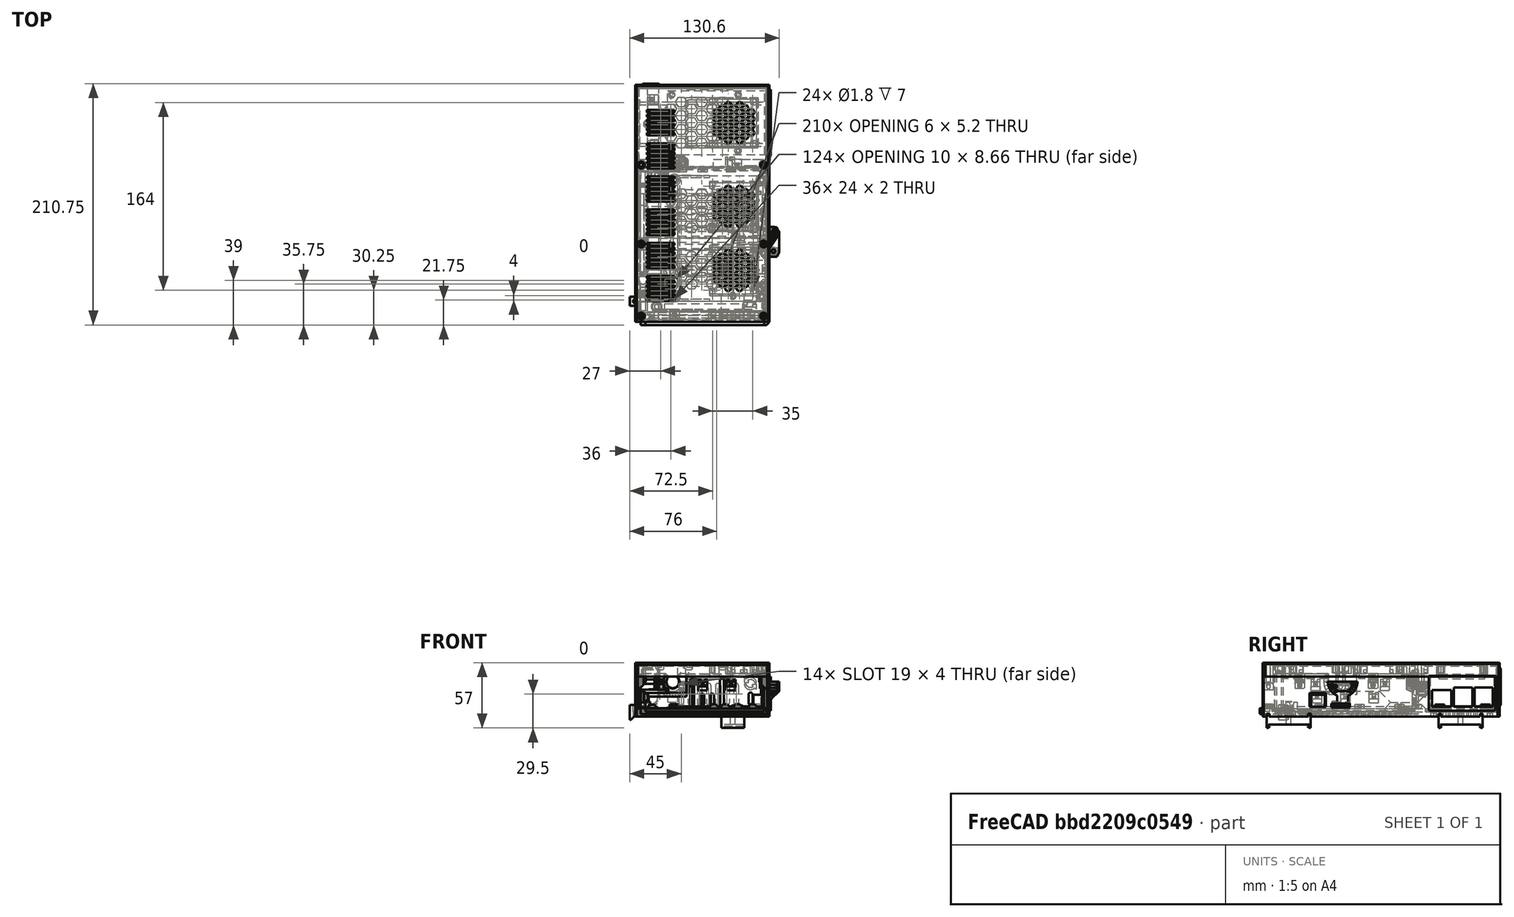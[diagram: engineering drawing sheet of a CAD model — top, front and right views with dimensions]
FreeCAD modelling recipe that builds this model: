
FCSTD DOCUMENT  (FreeCAD 0.18R16146 (Git))
Label: skr-case
License: All rights reserved
LicenseURL: http://en.wikipedia.org/wiki/All_rights_reserved
objects: Part::Feature×95, Part::Box×58, Part::MultiFuse×58, Part::Cylinder×45, Part::Cut×22, Part::Chamfer×17, Mesh::Feature×2, Part::Fillet×1
note: 296 computed .brp shape members not serialized (recipe doc carries the construction recipe); baked Part::Feature solids carry a one-line shape summary decoded from their .brp

FEATURE [Part::Feature] Cut003002  label="din-mount001"
  Placement = pos=(20,-18,-7) rot=(0,-1,0;1.5708rad)
  shape: bbox 20 x 38.4 x 12 mm, 68 faces (baked)
FEATURE [Part::Feature] Cut003002001  label="din-mount002"
  Placement = pos=(20,132,-7) rot=(0,-1,0;1.5708rad)
  shape: bbox 20 x 38.4 x 12 mm, 68 faces (baked)
FEATURE [Part::Box] Box  label="plate"
  AttacherType = Attacher::AttachEngine3D
  Height = 2
  Length = 84.3
  Width = 109.67
FEATURE [Part::Box] Box001  label="usb-pos"
  AttacherType = Attacher::AttachEngine3D
  Height = 10
  Length = 11.3
  Placement = pos=(73,24.11,2) rot=(0,0,1;0rad)
  Width = 11.98
FEATURE [Part::Box] Box002  label="sd-pos"
  AttacherType = Attacher::AttachEngine3D
  Height = 2
  Length = 13.3
  Placement = pos=(73,42.46,2) rot=(0,0,1;0rad)
  Width = 15.03
FEATURE [Part::Cylinder] Cylinder
  Angle = 360
  AttacherType = Attacher::AttachEngine3D
  Height = 10
  Placement = pos=(4.1,105.92,0) rot=(0,0,1;0rad)
  Radius = 1.65
FEATURE [Part::Cylinder] Cylinder001
  Angle = 360
  AttacherType = Attacher::AttachEngine3D
  Height = 10
  Placement = pos=(80.2,105.92,0) rot=(0,0,1;0rad)
  Radius = 1.65
FEATURE [Part::Cylinder] Cylinder002
  Angle = 360
  AttacherType = Attacher::AttachEngine3D
  Height = 10
  Placement = pos=(80.2,4.07,0) rot=(0,0,1;0rad)
  Radius = 1.65
FEATURE [Part::Cylinder] Cylinder003
  Angle = 360
  AttacherType = Attacher::AttachEngine3D
  Height = 10
  Placement = pos=(4.1,4.07,0) rot=(0,0,1;0rad)
  Radius = 1.65
FEATURE [Part::Cylinder] Cylinder004
  Angle = 360
  AttacherType = Attacher::AttachEngine3D
  Height = 10
  Placement = pos=(4.1,4.07,0) rot=(0,0,1;0rad)
  Radius = 2
FEATURE [Part::Cylinder] Cylinder005
  Angle = 360
  AttacherType = Attacher::AttachEngine3D
  Height = 10
  Placement = pos=(80.2,4.07,0) rot=(0,0,1;0rad)
  Radius = 2
FEATURE [Part::Cylinder] Cylinder006
  Angle = 360
  AttacherType = Attacher::AttachEngine3D
  Height = 10
  Placement = pos=(80.2,105.92,0) rot=(0,0,1;0rad)
  Radius = 2
FEATURE [Part::Cylinder] Cylinder007
  Angle = 360
  AttacherType = Attacher::AttachEngine3D
  Height = 10
  Placement = pos=(4.1,105.92,0) rot=(0,0,1;0rad)
  Radius = 2
FEATURE [Part::MultiFuse] Fusion  label="board-hole-pos"
  Shapes = -> [Cylinder003,Cylinder002,Cylinder001,Cylinder]
FEATURE [Part::Cut] Cut
  Base = -> Box
  Tool = -> Fusion
FEATURE [Part::Cylinder] Cylinder008
  Angle = 360
  AttacherType = Attacher::AttachEngine3D
  Height = 7
  Placement = pos=(80.2,105.92,0) rot=(0,0,1;0rad)
  Radius = 3.5
FEATURE [Part::Cylinder] Cylinder009
  Angle = 360
  AttacherType = Attacher::AttachEngine3D
  Height = 7
  Placement = pos=(80.2,4.07,0) rot=(0,0,1;0rad)
  Radius = 3.5
FEATURE [Part::Cylinder] Cylinder010
  Angle = 360
  AttacherType = Attacher::AttachEngine3D
  Height = 7
  Placement = pos=(4.1,4.07,0) rot=(0,0,1;0rad)
  Radius = 3.5
FEATURE [Part::Cylinder] Cylinder011
  Angle = 360
  AttacherType = Attacher::AttachEngine3D
  Height = 7
  Placement = pos=(4.1,105.92,0) rot=(0,0,1;0rad)
  Radius = 3.5
FEATURE [Part::MultiFuse] Fusion004  label="board-stand"
  Placement = pos=(30,0,0) rot=(0,0,1;0rad)
  Shapes = -> [Cylinder011,Cylinder010,Cylinder009,Cylinder008]
FEATURE [Part::MultiFuse] Fusion005  label="thread-insert"
  Placement = pos=(30,0,0) rot=(0,0,1;0rad)
  Shapes = -> [Cylinder006,Cylinder004,Cylinder005,Cylinder007]
FEATURE [Part::Box] Box003  label="main-plate"
  AttacherType = Attacher::AttachEngine3D
  Height = 4
  Length = 117
  Placement = pos=(0,-18,0) rot=(0,0,1;0rad)
  Width = 207
FEATURE [Part::Feature] Fusion010004007001  label="Bear-ref"
  Placement = pos=(60.6,53.5,2.3) rot=(0,0,1;0rad)
  shape: bbox 121 x 148.5 x 38 mm, 2925 faces, 7 solids (baked)
FEATURE [Part::Feature] Part__Feature001  label="zip-tie-slot"
  shape: bbox 8 x 9.5 x 3.5 mm, 30 faces (baked)
FEATURE [Part::Feature] Part__Feature001001  label="zip-tie-bed"
  Placement = pos=(64.5,-18,7) rot=(0,0,1;1.5708rad)
  shape: bbox 9.5 x 8 x 3.5 mm, 30 faces (baked)
FEATURE [Part::Feature] Part__Feature001002  label="zip-tie-power"
  Placement = pos=(77.5,-18,7) rot=(0,0,1;1.5708rad)
  shape: bbox 9.5 x 8 x 3.5 mm, 30 faces (baked)
FEATURE [Part::Feature] Part__Feature001004  label="zip-tie-e0"
  Placement = pos=(53.5,-18,7) rot=(0,0,1;1.5708rad)
  shape: bbox 9.5 x 8 x 3.5 mm, 30 faces (baked)
FEATURE [Part::Feature] Part__Feature001005  label="zip-tie-e1"
  Placement = pos=(43.5,-18,7) rot=(0,0,1;1.5708rad)
  shape: bbox 9.5 x 8 x 3.5 mm, 30 faces (baked)
FEATURE [Part::MultiFuse] Fusion010004007002  label="SKR-pref"
  Placement = pos=(30,0,7) rot=(0,0,1;0rad)
  Shapes = -> [Box001,Box002,Cut]
FEATURE [Part::Box] Box004  label="Cube"
  AttacherType = Attacher::AttachEngine3D
  Height = 2.4
  Length = 200
  Placement = pos=(0,-4.6,0) rot=(0,0,1;0rad)
  Width = 2.4
FEATURE [Part::Box] Box005  label="Cube001"
  AttacherType = Attacher::AttachEngine3D
  Height = 2.4
  Length = 200
  Placement = pos=(0,31.6,0) rot=(0,0,1;0rad)
  Width = 2.4
FEATURE [Part::Box] Box006  label="Cube002"
  AttacherType = Attacher::AttachEngine3D
  Height = 2.4
  Length = 200
  Placement = pos=(0,181.6,0) rot=(0,0,1;0rad)
  Width = 2.4
FEATURE [Part::Box] Box007  label="Cube003"
  AttacherType = Attacher::AttachEngine3D
  Height = 2.4
  Length = 200
  Placement = pos=(0,145.4,0) rot=(0,0,1;0rad)
  Width = 2.4
FEATURE [Part::Box] Box008  label="bottom-bar"
  AttacherType = Attacher::AttachEngine3D
  Height = 3
  Length = 117
  Placement = pos=(0,-18,4) rot=(0,0,1;0rad)
  Width = 10
FEATURE [Part::MultiFuse] Fusion010004007005  label="cable-mount"
  Placement = pos=(30,0,0) rot=(0,0,1;0rad)
  Shapes = -> [Part__Feature001005,Part__Feature001001,Part__Feature001002,Part__Feature001004]
FEATURE [Part::MultiFuse] Fusion010004007008
  Placement = pos=(75,5,0) rot=(0,0,1;0rad)
  Shapes = -> [Cut003002001,Cut003002]
FEATURE [Part::MultiFuse] Fusion010004007009
  Placement = pos=(0,-10,0) rot=(0,0,1;0rad)
  Shapes = -> [Box004,Box005,Box006,Box007]
FEATURE [Part::Box] Box009  label="Cube004"
  AttacherType = Attacher::AttachEngine3D
  Height = 2
  Length = 85
  Width = 56
FEATURE [Part::Cylinder] Cylinder012
  Angle = 360
  AttacherType = Attacher::AttachEngine3D
  Height = 10
  Placement = pos=(3.5,3.5,0) rot=(0,0,1;0rad)
  Radius = 1.35
FEATURE [Part::Cylinder] Cylinder013
  Angle = 360
  AttacherType = Attacher::AttachEngine3D
  Height = 10
  Placement = pos=(3.5,52.5,0) rot=(0,0,1;0rad)
  Radius = 1.35
FEATURE [Part::Cylinder] Cylinder014
  Angle = 360
  AttacherType = Attacher::AttachEngine3D
  Height = 10
  Placement = pos=(61.5,52.5,0) rot=(0,0,1;0rad)
  Radius = 1.35
FEATURE [Part::Cylinder] Cylinder015
  Angle = 360
  AttacherType = Attacher::AttachEngine3D
  Height = 10
  Placement = pos=(61.5,3.5,0) rot=(0,0,1;0rad)
  Radius = 1.35
FEATURE [Part::Cylinder] Cylinder016
  Angle = 360
  AttacherType = Attacher::AttachEngine3D
  Height = 10
  Placement = pos=(61.5,3.5,0) rot=(0,0,1;0rad)
  Radius = 1.45
FEATURE [Part::Cylinder] Cylinder017
  Angle = 360
  AttacherType = Attacher::AttachEngine3D
  Height = 10
  Placement = pos=(61.5,52.5,0) rot=(0,0,1;0rad)
  Radius = 1.45
FEATURE [Part::Cylinder] Cylinder018
  Angle = 360
  AttacherType = Attacher::AttachEngine3D
  Height = 10
  Placement = pos=(3.5,52.5,0) rot=(0,0,1;0rad)
  Radius = 1.45
FEATURE [Part::Cylinder] Cylinder019
  Angle = 360
  AttacherType = Attacher::AttachEngine3D
  Height = 10
  Placement = pos=(3.5,3.5,0) rot=(0,0,1;0rad)
  Radius = 1.45
FEATURE [Part::MultiFuse] Fusion010004007010
  Shapes = -> [Cylinder015,Cylinder014,Cylinder013,Cylinder012]
FEATURE [Part::Cut] Cut003002002  label="pi-pref"
  Base = -> Box009
  Placement = pos=(28,128,7) rot=(0,0,1;0rad)
  Tool = -> Fusion010004007010
FEATURE [Part::Box] Box010  label="wall-left"
  AttacherType = Attacher::AttachEngine3D
  Height = 35
  Length = 2
  Placement = pos=(0,-18,0) rot=(0,0,1;0rad)
  Width = 207
FEATURE [Part::Box] Box011  label="wall-right"
  AttacherType = Attacher::AttachEngine3D
  Height = 35
  Length = 2
  Placement = pos=(115,-18,0) rot=(0,0,1;0rad)
  Width = 207
FEATURE [Part::Box] Box012  label="wall-top"
  AttacherType = Attacher::AttachEngine3D
  Height = 35
  Length = 117
  Placement = pos=(0,187,0) rot=(0,0,1;0rad)
  Width = 2
FEATURE [Part::Box] Box013  label="sd-slot"
  AttacherType = Attacher::AttachEngine3D
  Height = 3.5
  Length = 4
  Placement = pos=(114,42,8) rot=(0,0,1;0rad)
  Width = 16
FEATURE [Part::Box] Box014  label="usb-slot"
  AttacherType = Attacher::AttachEngine3D
  Height = 12
  Length = 4
  Placement = pos=(114,23,8.5) rot=(0,0,1;0rad)
  Width = 14
FEATURE [Part::Box] Box016  label="Cube006"
  AttacherType = Attacher::AttachEngine3D
  Height = 34
  Length = 4
  Placement = pos=(114,128,5) rot=(0,0,1;0rad)
  Width = 56
FEATURE [Part::Feature] Part__Feature001006  label="zip-tie-slot001"
  Placement = pos=(20,-18,7) rot=(0,0,1;1.5708rad)
  shape: bbox 9.5 x 8 x 3.5 mm, 30 faces (baked)
FEATURE [Part::Feature] Part__Feature001007  label="zip-tie-slot002"
  Placement = pos=(39,-8,7) rot=(0,0,1;3.14159rad)
  shape: bbox 8 x 9.5 x 3.5 mm, 30 faces (baked)
FEATURE [Part::Box] Box017  label="Cube007"
  AttacherType = Attacher::AttachEngine3D
  Height = 13
  Length = 9
  Placement = pos=(-5,-4,-3) rot=(0,0,1;0rad)
  Width = 8
FEATURE [Part::Cylinder] Cylinder020
  Angle = 360
  AttacherType = Attacher::AttachEngine3D
  Height = 6
  Placement = pos=(0,0,4) rot=(0,0,1;0rad)
  Radius = 2
FEATURE [Part::Cylinder] Cylinder021
  Angle = 360
  AttacherType = Attacher::AttachEngine3D
  Height = 10
  Placement = pos=(0,0,-4) rot=(0,0,1;0rad)
  Radius = 1.7
FEATURE [Part::Chamfer] Chamfer
  Base = -> Box017
  Edges = 1 edges r=8: [Edge8]
FEATURE [Part::Chamfer] Chamfer001
  Base = -> Chamfer
  Edges = 2 edges r=2: [Edge1,Edge4]
FEATURE [Part::MultiFuse] Fusion010004007012
  Shapes = -> [Cylinder021,Cylinder020]
FEATURE [Part::Cut] Cut003002006  label="case-bolt"
  Base = -> Chamfer001
  Tool = -> Fusion010004007012
FEATURE [Part::Feature] Cut003002006001  label="case-bolt001"
  Placement = pos=(5,-13,25) rot=(0,0,1;0rad)
  shape: bbox 9 x 8 x 13 mm, 12 faces (baked)
FEATURE [Part::Feature] Cut003002006002  label="case-bolt002"
  Placement = pos=(112,-13,25) rot=(0,0,1;3.14159rad)
  shape: bbox 9 x 8 x 13 mm, 12 faces (baked)
FEATURE [Part::Feature] Cut003002006003  label="case-bolt003"
  Placement = pos=(112,50,25) rot=(0,0,1;3.14159rad)
  shape: bbox 9 x 8 x 13 mm, 12 faces (baked)
FEATURE [Part::Feature] Cut003002006004  label="case-bolt004"
  Placement = pos=(112,119,25) rot=(0,0,1;3.14159rad)
  shape: bbox 9 x 8 x 13 mm, 12 faces (baked)
FEATURE [Part::Feature] Cut003002006005  label="case-bolt005"
  Placement = pos=(5,50,25) rot=(0,0,1;0rad)
  shape: bbox 9 x 8 x 13 mm, 12 faces (baked)
FEATURE [Part::Feature] Cut003002006006  label="case-bolt006"
  Placement = pos=(5,119,25) rot=(0,0,1;0rad)
  shape: bbox 9 x 8 x 13 mm, 12 faces (baked)
FEATURE [Part::Feature] Part__Feature001009  label="zip-tie-slot004"
  Placement = pos=(20,27,7) rot=(0,0,1;1.5708rad)
  shape: bbox 9.5 x 8 x 3.5 mm, 30 faces (baked)
FEATURE [Part::Feature] Part__Feature001010  label="zip-tie-slot005"
  Placement = pos=(20,97,7) rot=(0,0,1;1.5708rad)
  shape: bbox 9.5 x 8 x 3.5 mm, 30 faces (baked)
FEATURE [Part::Feature] Part__Feature001011  label="zip-tie-slot006"
  Placement = pos=(20,62,7) rot=(0,0,1;1.5708rad)
  shape: bbox 9.5 x 8 x 3.5 mm, 30 faces (baked)
FEATURE [Part::Feature] Part__Feature001013  label="zip-tie-slot008"
  Placement = pos=(20,172,7) rot=(0,0,1;1.5708rad)
  shape: bbox 9.5 x 8 x 3.5 mm, 30 faces (baked)
FEATURE [Part::Box] Box018  label="bottom-bar001"
  AttacherType = Attacher::AttachEngine3D
  Height = 3
  Length = 10
  Placement = pos=(10.5,-18,4) rot=(0,0,1;0rad)
  Width = 206
FEATURE [Part::Box] Box019  label="mid-bar"
  AttacherType = Attacher::AttachEngine3D
  Height = 3
  Length = 117
  Placement = pos=(0,114,4) rot=(0,0,1;0rad)
  Width = 10
FEATURE [Part::Feature] Part__Feature001015  label="zip-tie-slot010"
  Placement = pos=(93.5,124,7) rot=(0,0,1;3.14159rad)
  shape: bbox 8 x 9.5 x 3.5 mm, 30 faces (baked)
FEATURE [Part::Feature] Part__Feature001016  label="zip-tie-slot011"
  Placement = pos=(20,132,7) rot=(0,0,1;1.5708rad)
  shape: bbox 9.5 x 8 x 3.5 mm, 30 faces (baked)
FEATURE [Part::MultiFuse] Fusion010004007014
  Shapes = -> [Cut003002006001,Cut003002006005,Cut003002006006,Cut003002006002,Cut003002006003,Cut003002006004]
FEATURE [Part::Box] Box020  label="Cube008"
  AttacherType = Attacher::AttachEngine3D
  Height = 10
  Length = 11
  Placement = pos=(10,141,5) rot=(0,0,1;0rad)
  Width = 31
FEATURE [Part::Feature] Body001  label="m2.6"
  shape: bbox 5.7 x 4.936 x 5 mm, 8 faces (baked)
FEATURE [Part::Feature] Body002  label="m2.007"
  Placement = pos=(0,49,0) rot=(0,0,1;0rad)
  shape: bbox 5.7 x 4.936 x 5 mm, 8 faces (baked)
FEATURE [Part::Feature] Body003  label="m2.008"
  Placement = pos=(58,49,0) rot=(0,0,1;0rad)
  shape: bbox 5.7 x 4.936 x 5 mm, 8 faces (baked)
FEATURE [Part::Feature] Body004  label="m2.009"
  Placement = pos=(58,0,0) rot=(0,0,1;0rad)
  shape: bbox 5.7 x 4.936 x 5 mm, 8 faces (baked)
FEATURE [Part::MultiFuse] Fusion010004007019
  Shapes = -> [Body004,Body003,Body002,Body001]
FEATURE [Part::Cylinder] Cylinder022
  Angle = 360
  AttacherType = Attacher::AttachEngine3D
  Height = 7
  Placement = pos=(3.5,3.5,0) rot=(0,0,1;0rad)
  Radius = 3
FEATURE [Part::Cylinder] Cylinder023
  Angle = 360
  AttacherType = Attacher::AttachEngine3D
  Height = 7
  Placement = pos=(3.5,52.5,0) rot=(0,0,1;0rad)
  Radius = 3
FEATURE [Part::Cylinder] Cylinder024
  Angle = 360
  AttacherType = Attacher::AttachEngine3D
  Height = 7
  Placement = pos=(61.5,3.5,0) rot=(0,0,1;0rad)
  Radius = 3
FEATURE [Part::Cylinder] Cylinder025
  Angle = 360
  AttacherType = Attacher::AttachEngine3D
  Height = 7
  Placement = pos=(61.5,52.5,0) rot=(0,0,1;0rad)
  Radius = 3
FEATURE [Part::MultiFuse] Fusion010004007020
  Placement = pos=(28,128,0) rot=(0,0,1;0rad)
  Shapes = -> [Cylinder025,Cylinder024,Cylinder023,Cylinder022]
FEATURE [Part::MultiFuse] Fusion010004007021
  Placement = pos=(-3.5,-3.5,0) rot=(0,0,1;0rad)
  Shapes = -> [Cylinder019,Cylinder016,Cylinder018,Cylinder017]
FEATURE [Part::MultiFuse] Fusion010004007022
  Placement = pos=(31.5,131.5,-2) rot=(0,0,1;0rad)
  Shapes = -> [Fusion010004007021,Fusion010004007019]
FEATURE [Part::Cut] Cut003002006008
  Base = -> Box018
  Tool = -> Box020
FEATURE [Part::Cylinder] Cylinder026
  Angle = 360
  AttacherType = Attacher::AttachEngine3D
  Height = 10
  Placement = pos=(10,4.7,0) rot=(0,0,1;0rad)
  Radius = 1.65
FEATURE [Part::Cylinder] Cylinder027
  Angle = 360
  AttacherType = Attacher::AttachEngine3D
  Height = 10
  Placement = pos=(10,4.7,3) rot=(0,0,1;0rad)
  Radius = 3
FEATURE [Part::MultiFuse] Fusion010004007026  label="case-bolt007"
  Shapes = -> [Cylinder027,Cylinder026]
FEATURE [Part::Feature] Fusion010004007026001  label="case-bolt008"
  shape: bbox 6 x 6 x 13 mm, 5 faces (baked)
FEATURE [Part::Feature] Fusion010004007026002  label="case-bolt009"
  Placement = pos=(0,150,0) rot=(0,0,1;0rad)
  shape: bbox 6 x 6 x 13 mm, 5 faces (baked)
FEATURE [Part::Feature] Fusion010004007026003  label="case-bolt010"
  Placement = pos=(75,150,0) rot=(0,0,1;0rad)
  shape: bbox 6 x 6 x 13 mm, 5 faces (baked)
FEATURE [Part::Feature] Fusion010004007026004  label="case-bolt011"
  Placement = pos=(75,0,0) rot=(0,0,1;0rad)
  shape: bbox 6 x 6 x 13 mm, 5 faces (baked)
FEATURE [Part::MultiFuse] Fusion010004007026005
  Shapes = -> [Fusion010004007026004,Fusion010004007026003,Fusion010004007026002,Fusion010004007026001]
FEATURE [Part::MultiFuse] Fusion010004007026006
  Shapes = -> [Part__Feature001006,Part__Feature001007,Part__Feature001015,Part__Feature001009,Part__Feature001010,Part__Feature001013,Part__Feature001011,Part__Feature001016]
FEATURE [Part::Feature] Body005  label="Body001"
  Placement = pos=(31,16,0) rot=(0,0,1;0rad)
  shape: bbox 10 x 8.66 x 10 mm, 8 faces (baked)
FEATURE [Part::Feature] Body006  label="Body002"
  Placement = pos=(31,28,0) rot=(0,0,1;0rad)
  shape: bbox 10 x 8.66 x 10 mm, 8 faces (baked)
FEATURE [Part::Feature] Body007  label="Body003"
  Placement = pos=(31,40,0) rot=(0,0,1;0rad)
  shape: bbox 10 x 8.66 x 10 mm, 8 faces (baked)
FEATURE [Part::Feature] Body008  label="Body004"
  Placement = pos=(40,34,0) rot=(0,0,1;0rad)
  shape: bbox 10 x 8.66 x 10 mm, 8 faces (baked)
FEATURE [Part::Feature] Body009  label="Body005"
  Placement = pos=(40,22,0) rot=(0,0,1;0rad)
  shape: bbox 10 x 8.66 x 10 mm, 8 faces (baked)
FEATURE [Part::MultiFuse] Fusion010004007026008
  Shapes = -> [Body007,Body006,Body005]
FEATURE [Part::MultiFuse] Fusion010004007026009
  Shapes = -> [Body008,Body009]
FEATURE [Part::Feature] Fusion010004007026009001  label="Fusion010004007026010"
  Placement = pos=(18,0,0) rot=(0,0,1;0rad)
  shape: bbox 10 x 20.66 x 10 mm, 16 faces, 2 solids (baked)
FEATURE [Part::Feature] Fusion010004007026008001  label="Fusion010004007026011"
  Placement = pos=(18,0,0) rot=(0,0,1;0rad)
  shape: bbox 10 x 32.66 x 10 mm, 24 faces, 3 solids (baked)
FEATURE [Part::Feature] Fusion010004007026009002  label="Fusion010004007026012"
  Placement = pos=(36,0,0) rot=(0,0,1;0rad)
  shape: bbox 10 x 32.66 x 10 mm, 24 faces, 3 solids (baked)
FEATURE [Part::Feature] Fusion010004007026009003  label="Fusion010004007026013"
  Placement = pos=(36,0,0) rot=(0,0,1;0rad)
  shape: bbox 10 x 20.66 x 10 mm, 16 faces, 2 solids (baked)
FEATURE [Part::Feature] Fusion010004007026009004  label="Fusion010004007026014"
  Placement = pos=(54,0,0) rot=(0,0,1;0rad)
  shape: bbox 10 x 20.66 x 10 mm, 16 faces, 2 solids (baked)
FEATURE [Part::Feature] Fusion010004007026009005  label="Fusion010004007026015"
  Placement = pos=(54,0,0) rot=(0,0,1;0rad)
  shape: bbox 10 x 32.66 x 10 mm, 24 faces, 3 solids (baked)
FEATURE [Part::Feature] Fusion010004007026009006  label="Fusion010004007026016"
  Placement = pos=(72,0,0) rot=(0,0,1;0rad)
  shape: bbox 10 x 32.66 x 10 mm, 24 faces, 3 solids (baked)
FEATURE [Part::Feature] Body010  label="Body006"
  Placement = pos=(31,142,0) rot=(0,0,1;0rad)
  shape: bbox 10 x 8.66 x 10 mm, 8 faces (baked)
FEATURE [Part::MultiFuse] Fusion010004007026009007
  Placement = pos=(0,-1,0) rot=(0,0,1;0rad)
  Shapes = -> [Fusion010004007026008,Fusion010004007026009002,Fusion010004007026009003,Fusion010004007026009001,Fusion010004007026009004,Fusion010004007026009006,Fusion010004007026009005,Fusion010004007026009,Fusion010004007026008001]
FEATURE [Part::Feature] Fusion010004007026009007001  label="Fusion010004007026009008"
  Placement = pos=(0,45,0) rot=(0,0,1;0rad)
  shape: bbox 82 x 32.66 x 10 mm, 184 faces, 23 solids (baked)
FEATURE [Part::Feature] Body011  label="Body007"
  Placement = pos=(40,91,0) rot=(0,0,1;0rad)
  shape: bbox 10 x 8.66 x 10 mm, 8 faces (baked)
FEATURE [Part::Feature] Body012  label="Body008"
  Placement = pos=(58,91,0) rot=(0,0,1;0rad)
  shape: bbox 10 x 8.66 x 10 mm, 8 faces (baked)
FEATURE [Part::Feature] Body013  label="Body009"
  Placement = pos=(76,91,0) rot=(0,0,1;0rad)
  shape: bbox 10 x 8.66 x 10 mm, 8 faces (baked)
FEATURE [Part::Feature] Body014  label="Body010"
  Placement = pos=(94,91,0) rot=(0,0,1;0rad)
  shape: bbox 10 x 8.66 x 10 mm, 8 faces (baked)
FEATURE [Part::MultiFuse] Fusion010004007026009007002
  Placement = pos=(0,3,0) rot=(0,0,1;0rad)
  Shapes = -> [Body014,Body013,Body012,Body011,Fusion010004007026009007001]
FEATURE [Part::Feature] Body015  label="Body011"
  Placement = pos=(31,154,0) rot=(0,0,1;0rad)
  shape: bbox 10 x 8.66 x 10 mm, 8 faces (baked)
FEATURE [Part::Feature] Body016  label="Body012"
  Placement = pos=(31,166,0) rot=(0,0,1;0rad)
  shape: bbox 10 x 8.66 x 10 mm, 8 faces (baked)
FEATURE [Part::Feature] Body017  label="Body013"
  Placement = pos=(40,160,0) rot=(0,0,1;0rad)
  shape: bbox 10 x 8.66 x 10 mm, 8 faces (baked)
FEATURE [Part::Feature] Body018  label="Body014"
  Placement = pos=(40,148,0) rot=(0,0,1;0rad)
  shape: bbox 10 x 8.66 x 10 mm, 8 faces (baked)
FEATURE [Part::Feature] Body019  label="Body015"
  Placement = pos=(40,136,0) rot=(0,0,1;0rad)
  shape: bbox 10 x 8.66 x 10 mm, 8 faces (baked)
FEATURE [Part::Feature] Body020  label="Body016"
  Placement = pos=(40,172,0) rot=(0,0,1;0rad)
  shape: bbox 10 x 8.66 x 10 mm, 8 faces (baked)
FEATURE [Part::MultiFuse] Fusion010004007026009007003
  Placement = pos=(0,2,0) rot=(0,0,1;0rad)
  Shapes = -> [Body020,Body017,Body018,Body019]
FEATURE [Part::MultiFuse] Fusion010004007026009007004
  Placement = pos=(0,2,0) rot=(0,0,1;0rad)
  Shapes = -> [Body016,Body015,Body010]
FEATURE [Part::Feature] Fusion010004007026009007004001  label="Fusion010004007026009007005"
  Placement = pos=(18,2,0) rot=(0,0,1;0rad)
  shape: bbox 10 x 32.66 x 10 mm, 24 faces, 3 solids (baked)
FEATURE [Part::Feature] Fusion010004007026009007003001  label="Fusion010004007026009007006"
  Placement = pos=(18,2,0) rot=(0,0,1;0rad)
  shape: bbox 10 x 44.66 x 10 mm, 32 faces, 4 solids (baked)
FEATURE [Part::Feature] Fusion010004007026009007004002  label="Fusion010004007026009007007"
  Placement = pos=(36,2,0) rot=(0,0,1;0rad)
  shape: bbox 10 x 44.66 x 10 mm, 32 faces, 4 solids (baked)
FEATURE [Part::Feature] Fusion010004007026009007004003  label="Fusion010004007026009007008"
  Placement = pos=(36,2,0) rot=(0,0,1;0rad)
  shape: bbox 10 x 32.66 x 10 mm, 24 faces, 3 solids (baked)
FEATURE [Part::MultiFuse] Fusion010004007026009007004004
  Shapes = -> [Fusion010004007026009007004003,Fusion010004007026009007004002,Fusion010004007026009007003001,Fusion010004007026009007004001,Fusion010004007026009007004,Fusion010004007026009007003]
FEATURE [Part::MultiFuse] Fusion010004007026009007004005
  Shapes = -> [Fusion010004007026009007004004,Fusion010004007026009007002,Fusion010004007026009007]
FEATURE [Part::Box] Box021  label="Cube009"
  AttacherType = Attacher::AttachEngine3D
  Height = 5
  Length = 117
  Placement = pos=(0,45,0) rot=(0,0,1;0rad)
  Width = 10
FEATURE [Part::Cylinder] Cylinder028
  Angle = 360
  AttacherType = Attacher::AttachEngine3D
  Height = 10
  Placement = pos=(13.5,184,17) rot=(-1,0,0;1.5708rad)
  Radius = 6
FEATURE [Part::Box] Box022  label="Cube010"
  AttacherType = Attacher::AttachEngine3D
  Height = 18
  Length = 12
  Placement = pos=(7.5,184,17) rot=(0,0,1;0rad)
  Width = 10
FEATURE [Part::Box] Box023  label="Cube011"
  AttacherType = Attacher::AttachEngine3D
  Height = 18
  Length = 12
  Placement = pos=(7.5,184,17) rot=(0,0,1;0rad)
  Width = 10
FEATURE [Part::Cylinder] Cylinder029
  Angle = 360
  AttacherType = Attacher::AttachEngine3D
  Height = 10
  Placement = pos=(13.5,184,17) rot=(-1,0,0;1.5708rad)
  Radius = 6
FEATURE [Part::MultiFuse] Fusion010004007026009007004007
  Shapes = -> [Box022,Cylinder028]
FEATURE [Part::Cylinder] Cylinder030
  Angle = 360
  AttacherType = Attacher::AttachEngine3D
  Height = 4
  Placement = pos=(13.5,186,17) rot=(-1,0,0;1.5708rad)
  Radius = 8
FEATURE [Part::Box] Box024  label="Cube012"
  AttacherType = Attacher::AttachEngine3D
  Height = 18
  Length = 16
  Placement = pos=(5.5,186,17) rot=(0,0,1;0rad)
  Width = 4
FEATURE [Part::Chamfer] Chamfer004
  Base = -> Box024
  Edges = 4 edges r=1: [Edge1,Edge3,Edge5,Edge7]
FEATURE [Part::Chamfer] Chamfer005
  Base = -> Cylinder030
  Edges = 2 edges r=1: [Edge1,Edge3]
FEATURE [Part::MultiFuse] Fusion010004007026009007004008
  Shapes = -> [Chamfer004,Chamfer005]
FEATURE [Part::MultiFuse] Fusion010004007026009007004009
  Shapes = -> [Cylinder029,Box023]
FEATURE [Part::Cut] Cut003002006013003
  Base = -> Fusion010004007026009007004008
  Tool = -> Fusion010004007026009007004009
FEATURE [Part::Cylinder] Cylinder031
  Angle = 360
  AttacherType = Attacher::AttachEngine3D
  Height = 10
  Placement = pos=(40,183,10) rot=(-1,0,0;1.5708rad)
  Radius = 2
FEATURE [Part::Cylinder] Cylinder032
  Angle = 360
  AttacherType = Attacher::AttachEngine3D
  Height = 10
  Placement = pos=(40,183,25) rot=(-1,0,0;1.5708rad)
  Radius = 2
FEATURE [Part::Box] Box025  label="Cube013"
  AttacherType = Attacher::AttachEngine3D
  Height = 15
  Length = 4
  Placement = pos=(38,183,10) rot=(0,0,1;0rad)
  Width = 10
FEATURE [Part::MultiFuse] Fusion010004007026009007004010
  Placement = pos=(0,0,2) rot=(0,0,1;0rad)
  Shapes = -> [Box025,Cylinder032,Cylinder031]
FEATURE [Part::Feature] Fusion010004007026009007004010001  label="Fusion010004007026009007004011"
  Placement = pos=(8,0,2) rot=(0,0,1;0rad)
  shape: bbox 4 x 10 x 19 mm, 14 faces (baked)
FEATURE [Part::Feature] Fusion010004007026009007004010002  label="Fusion010004007026009007004012"
  Placement = pos=(16,0,2) rot=(0,0,1;0rad)
  shape: bbox 4 x 10 x 19 mm, 14 faces (baked)
FEATURE [Part::Feature] Fusion010004007026009007004010003  label="Fusion010004007026009007004013"
  Placement = pos=(24,0,2) rot=(0,0,1;0rad)
  shape: bbox 4 x 10 x 19 mm, 14 faces (baked)
FEATURE [Part::Feature] Fusion010004007026009007004010004  label="Fusion010004007026009007004014"
  Placement = pos=(32,0,2) rot=(0,0,1;0rad)
  shape: bbox 4 x 10 x 19 mm, 14 faces (baked)
FEATURE [Part::Feature] Fusion010004007026009007004010005  label="Fusion010004007026009007004015"
  Placement = pos=(40,0,2) rot=(0,0,1;0rad)
  shape: bbox 4 x 10 x 19 mm, 14 faces (baked)
FEATURE [Part::Feature] Fusion010004007026009007004010006  label="Fusion010004007026009007004016"
  Placement = pos=(48,0,2) rot=(0,0,1;0rad)
  shape: bbox 4 x 10 x 19 mm, 14 faces (baked)
FEATURE [Part::MultiFuse] Fusion010004007026009007004010008
  Shapes = -> [Box011,Box012,Box010,Box003]
FEATURE [Part::Chamfer] Chamfer006
  Base = -> Fusion010004007026009007004010008
  Edges = 5 edges r=1: [Edge27,Edge28,Edge29,Edge30,Edge45]
FEATURE [Part::MultiFuse] Fusion010004007026009007004010009  label="side-cut"
  Shapes = -> [Box014,Box013,Box016]
FEATURE [Part::Cut] Cut003002006013004
  Base = -> Chamfer006
  Tool = -> Fusion010004007026009007004010009
FEATURE [Part::Box] Box026  label="Cube014"
  AttacherType = Attacher::AttachEngine3D
  Height = 10
  Length = 40
  Placement = pos=(28,113,4) rot=(0,0,1;0rad)
  Width = 12
FEATURE [Part::Cut] Cut003002006013005
  Base = -> Box019
  Tool = -> Box026
FEATURE [Part::MultiFuse] Fusion010004007026009007004010010
  Shapes = -> [Box008,Cut003002006008,Box021,Cut003002006013005]
FEATURE [Part::MultiFuse] Fusion010004007026009007004010011
  Shapes = -> [Cut003002006013004,Fusion010004007026009007004010010]
FEATURE [Part::MultiFuse] Fusion010004007026009007004010012
  Shapes = -> [Fusion010004007005,Fusion010004007026006]
FEATURE [Part::MultiFuse] Fusion010004007026009007004010013
  Shapes = -> [Fusion010004007026009007004010012,Fusion010004007026009007004010011]
FEATURE [Part::MultiFuse] Fusion010004007026009007004010014
  Shapes = -> [Fusion010004007026009007004010013,Fusion010004007014]
FEATURE [Part::MultiFuse] Fusion010004007026009007004010015
  Shapes = -> [Fusion010004007026009007004010,Fusion010004007026009007004010001,Fusion010004007026009007004010002,Fusion010004007026009007004010003,Fusion010004007026009007004010004,Fusion010004007026009007004010005,Fusion010004007026009007004010006]
FEATURE [Part::MultiFuse] Fusion010004007026009007004010016
  Shapes = -> [Fusion010004007026009007004010014,Fusion004]
FEATURE [Part::Cut] Cut003002006013006
  Base = -> Fusion010004007026009007004010016
  Tool = -> Fusion005
FEATURE [Part::MultiFuse] Fusion010004007026009007004010017
  Shapes = -> [Fusion010004007020,Cut003002006013006]
FEATURE [Part::Cut] Cut003002006013007
  Base = -> Fusion010004007026009007004010017
  Tool = -> Fusion010004007022
FEATURE [Part::Cut] Cut003002006013008
  Base = -> Cut003002006013007
  Tool = -> Fusion010004007026005
FEATURE [Part::MultiFuse] Fusion010004007026009007004010018
  Shapes = -> [Cut003002006013008,Cut003002006013003]
FEATURE [Part::Cut] Cut003002006013009
  Base = -> Fusion010004007026009007004010018
  Tool = -> Fusion010004007026009007004007
FEATURE [Part::Cut] Cut003002006013010
  Base = -> Cut003002006013009
  Tool = -> Fusion010004007026009007004010015
FEATURE [Part::Cut] Cut003002006013011
  Base = -> Cut003002006013010
  Tool = -> Fusion010004007026009007004005
FEATURE [Part::Cut] Cut003002006013012
  Base = -> Cut003002006013011
  Tool = -> Fusion010004007009
FEATURE [Part::Feature] Cut003002006013012001  label="Cut003002006013013"
  shape: bbox 117 x 208 x 35 mm, 1048 faces (baked)
FEATURE [Part::Chamfer] Chamfer007
  Base = -> Cut003002006013012001
  Edges = 2 edges r=1: [Edge2931,Edge2932]
FEATURE [Part::Chamfer] Chamfer008
  Base = -> Chamfer007
  Edges = 2 edges r=2: [Edge19,Edge51]
FEATURE [Part::Box] Box027  label="Cube015"
  AttacherType = Attacher::AttachEngine3D
  Height = 29.75
  Length = 4
  Placement = pos=(114,128.25,5.25) rot=(0,0,1;0rad)
  Width = 55.5
FEATURE [Part::Box] Box028  label="Cube016"
  AttacherType = Attacher::AttachEngine3D
  Height = 30
  Length = 1
  Placement = pos=(117.25,127,5) rot=(0,0,1;0rad)
  Width = 58
FEATURE [Part::Box] Box029  label="Cube017"
  AttacherType = Attacher::AttachEngine3D
  Height = 30
  Length = 1
  Placement = pos=(113.75,127,5) rot=(0,0,1;0rad)
  Width = 58
FEATURE [Part::Chamfer] Chamfer010
  Base = -> Box028
  Edges = 4 edges r=1: [Edge9,Edge10,Edge11,Edge12]
FEATURE [Part::Chamfer] Chamfer011
  Base = -> Box029
  Edges = 4 edges r=1: [Edge9,Edge10,Edge11,Edge12]
FEATURE [Part::Box] Box030  label="lan"
  AttacherType = Attacher::AttachEngine3D
  Height = 14.5
  Length = 11
  Placement = pos=(111,129.75,9) rot=(0,0,1;0rad)
  Width = 17
FEATURE [Part::Box] Box032  label="usb2"
  AttacherType = Attacher::AttachEngine3D
  Height = 17
  Length = 13
  Placement = pos=(111,167,9) rot=(0,0,1;0rad)
  Width = 16
FEATURE [Part::Box] Box033  label="usb1"
  AttacherType = Attacher::AttachEngine3D
  Height = 17
  Length = 13
  Placement = pos=(111,149,9) rot=(0,0,1;0rad)
  Width = 16
FEATURE [Part::Chamfer] Chamfer012
  Base = -> Box027
  Edges = 4 edges r=1: [Edge9,Edge10,Edge11,Edge12]
FEATURE [Part::MultiFuse] Fusion010004007026009007004010021
  Shapes = -> [Chamfer012,Chamfer010,Chamfer011]
FEATURE [Part::MultiFuse] Fusion010004007026009007004010022
  Placement = pos=(0,0,-0.5) rot=(0,0,1;0rad)
  Shapes = -> [Box033,Box032,Box030]
FEATURE [Part::Cut] Cut003002006013012002
  Base = -> Fusion010004007026009007004010021
  Tool = -> Fusion010004007026009007004010022
FEATURE [Mesh::Feature] skrpref
  Placement = pos=(72,55,7) rot=(0,0,1;1.5708rad)
FEATURE [Mesh::Feature] pi_pref  label="pi-pref001"
  Placement = pos=(28.5,128,7.5) rot=(0,0,1;0rad)
FEATURE [Part::Feature] Fusion001011001  label="fan-slot"
  Placement = pos=(89,24,36) rot=(0,0,1;0rad)
  shape: bbox 42 x 44 x 12 mm, 254 faces (baked)
FEATURE [Part::Feature] Fusion010004007026009007004010023  label="fan-slot001"
  Placement = pos=(89,80,36) rot=(0,0,1;0rad)
  shape: bbox 42 x 44 x 12 mm, 254 faces (baked)
FEATURE [Part::Feature] Fusion010004007026009007004010024  label="fan-slot002"
  Placement = pos=(89,153,36) rot=(0,0,1;0rad)
  shape: bbox 42 x 44 x 12 mm, 254 faces (baked)
FEATURE [Part::Box] Box034  label="Cube018"
  AttacherType = Attacher::AttachEngine3D
  Height = 2
  Length = 117
  Placement = pos=(0,-18,45) rot=(0,0,1;0rad)
  Width = 207
FEATURE [Part::Box] Box035  label="Cube019"
  AttacherType = Attacher::AttachEngine3D
  Height = 3
  Length = 42
  Placement = pos=(65,5,45) rot=(0,0,1;0rad)
  Width = 44
FEATURE [Part::Box] Box036  label="Cube020"
  AttacherType = Attacher::AttachEngine3D
  Height = 3
  Length = 42
  Placement = pos=(65,61,45) rot=(0,0,1;0rad)
  Width = 44
FEATURE [Part::Box] Box037  label="Cube021"
  AttacherType = Attacher::AttachEngine3D
  Height = 3
  Length = 42
  Placement = pos=(65,134,45) rot=(0,0,1;0rad)
  Width = 44
FEATURE [Part::MultiFuse] Fusion010004007026009007004010025
  Shapes = -> [Box037,Box036,Box035]
FEATURE [Part::Box] Box038  label="Cube022"
  AttacherType = Attacher::AttachEngine3D
  Height = 10
  Length = 2
  Placement = pos=(0,-18,35) rot=(0,0,1;0rad)
  Width = 207
FEATURE [Part::Box] Box039  label="Cube023"
  AttacherType = Attacher::AttachEngine3D
  Height = 10
  Length = 2
  Placement = pos=(115,-18,35) rot=(0,0,1;0rad)
  Width = 207
FEATURE [Part::Box] Box040  label="Cube024"
  AttacherType = Attacher::AttachEngine3D
  Height = 10
  Length = 117
  Placement = pos=(0,187,35) rot=(0,0,1;0rad)
  Width = 2
FEATURE [Part::Box] Box041  label="Cube025"
  AttacherType = Attacher::AttachEngine3D
  Height = 10
  Length = 117
  Placement = pos=(0,-18,35) rot=(0,0,1;0rad)
  Width = 2
FEATURE [Part::Cut] Cut003002006013012003
  Base = -> Box034
  Tool = -> Fusion010004007026009007004010025
FEATURE [Part::MultiFuse] Fusion010004007026009007004010026
  Placement = pos=(0,0,-1) rot=(0,0,1;0rad)
  Shapes = -> [Fusion001011001,Fusion010004007026009007004010024,Fusion010004007026009007004010023]
FEATURE [Part::Box] Box042  label="Cube026"
  AttacherType = Attacher::AttachEngine3D
  Height = 10
  Length = 2
  Placement = pos=(37,0,35) rot=(0,0,1;0rad)
  Width = 110
FEATURE [Part::Box] Box043  label="Cube027"
  AttacherType = Attacher::AttachEngine3D
  Height = 10
  Length = 2
  Placement = pos=(44,134,35) rot=(0,0,1;0rad)
  Width = 44
FEATURE [Part::Box] Box044  label="Cube028"
  AttacherType = Attacher::AttachEngine3D
  Height = 10
  Length = 28
  Placement = pos=(37,0,35) rot=(0,0,1;0rad)
  Width = 2
FEATURE [Part::Box] Box045  label="Cube029"
  AttacherType = Attacher::AttachEngine3D
  Height = 10
  Length = 28
  Placement = pos=(37,108,35) rot=(0,0,1;0rad)
  Width = 2
FEATURE [Part::Box] Box046  label="Cube030"
  AttacherType = Attacher::AttachEngine3D
  Height = 10
  Length = 21
  Placement = pos=(44,134,35) rot=(0,0,1;0rad)
  Width = 2
FEATURE [Part::Box] Box047  label="Cube031"
  AttacherType = Attacher::AttachEngine3D
  Height = 10
  Length = 21
  Placement = pos=(44,176,35) rot=(0,0,1;0rad)
  Width = 2
FEATURE [Part::Box] Box048  label="Cube032"
  AttacherType = Attacher::AttachEngine3D
  Height = 0.5
  Length = 2
  Placement = pos=(115,127,35) rot=(0,0,1;0rad)
  Width = 58
FEATURE [Part::Cut] Cut003002006013012004
  Base = -> Box039
  Tool = -> Box048
FEATURE [Part::MultiFuse] Fusion010004007026009007004010027
  Shapes = -> [Cut003002006013012003,Box043,Box042]
FEATURE [Part::Fillet] Fillet
  Base = -> Fusion010004007026009007004010027
  Edges = 2 edges r=9: [Edge31,Edge35]
FEATURE [Part::Cylinder] Cylinder033
  Angle = 360
  AttacherType = Attacher::AttachEngine3D
  Height = 10
  Placement = pos=(5,-13,43) rot=(0,0,1;0rad)
  Radius = 1.65
FEATURE [Part::Cylinder] Cylinder034
  Angle = 360
  AttacherType = Attacher::AttachEngine3D
  Height = 10
  Placement = pos=(112,-13,43) rot=(0,0,1;0rad)
  Radius = 1.65
FEATURE [Part::Cylinder] Cylinder035
  Angle = 360
  AttacherType = Attacher::AttachEngine3D
  Height = 10
  Placement = pos=(112,50,43) rot=(0,0,1;0rad)
  Radius = 1.65
FEATURE [Part::Cylinder] Cylinder036
  Angle = 360
  AttacherType = Attacher::AttachEngine3D
  Height = 10
  Placement = pos=(5,50,43) rot=(0,0,1;0rad)
  Radius = 1.65
FEATURE [Part::Cylinder] Cylinder037
  Angle = 360
  AttacherType = Attacher::AttachEngine3D
  Height = 10
  Placement = pos=(5,119,43) rot=(0,0,1;0rad)
  Radius = 1.65
FEATURE [Part::Cylinder] Cylinder038
  Angle = 360
  AttacherType = Attacher::AttachEngine3D
  Height = 10
  Placement = pos=(112,119,43) rot=(0,0,1;0rad)
  Radius = 1.65
FEATURE [Part::Box] Box049  label="Cube033"
  AttacherType = Attacher::AttachEngine3D
  Height = 10
  Length = 8
  Placement = pos=(1,-17,35) rot=(0,0,1;0rad)
  Width = 8
FEATURE [Part::Chamfer] Chamfer013
  Base = -> Box049
  Edges = 2 edges r=2: [Edge5,Edge7]
FEATURE [Part::Feature] Chamfer013001  label="Chamfer014"
  Placement = pos=(0,63,0) rot=(0,0,1;0rad)
  shape: bbox 8 x 8 x 10 mm, 8 faces (baked)
FEATURE [Part::Feature] Chamfer013002  label="Chamfer015"
  Placement = pos=(0,132,0) rot=(0,0,1;0rad)
  shape: bbox 8 x 8 x 10 mm, 8 faces (baked)
FEATURE [Part::Feature] Chamfer013003  label="Chamfer016"
  Placement = pos=(117,106,0) rot=(0,0,1;3.14159rad)
  shape: bbox 8 x 8 x 10 mm, 8 faces (baked)
FEATURE [Part::Feature] Chamfer013004  label="Chamfer017"
  Placement = pos=(117,37,0) rot=(0,0,1;3.14159rad)
  shape: bbox 8 x 8 x 10 mm, 8 faces (baked)
FEATURE [Part::Feature] Chamfer013005  label="Chamfer018"
  Placement = pos=(117,-26,0) rot=(0,0,1;3.14159rad)
  shape: bbox 8 x 8 x 10 mm, 8 faces (baked)
FEATURE [Part::MultiFuse] Fusion010004007026009007004010028
  Shapes = -> [Chamfer013005,Chamfer013004,Chamfer013003,Chamfer013002,Chamfer013001,Chamfer013]
FEATURE [Part::Cylinder] Cylinder039
  Angle = 360
  AttacherType = Attacher::AttachEngine3D
  Height = 10
  Placement = pos=(112,119,43) rot=(0,0,1;0rad)
  Radius = 3
FEATURE [Part::Cylinder] Cylinder040
  Angle = 360
  AttacherType = Attacher::AttachEngine3D
  Height = 10
  Placement = pos=(5,119,43) rot=(0,0,1;0rad)
  Radius = 3
FEATURE [Part::Cylinder] Cylinder041
  Angle = 360
  AttacherType = Attacher::AttachEngine3D
  Height = 10
  Placement = pos=(112,50,43) rot=(0,0,1;0rad)
  Radius = 3
FEATURE [Part::Cylinder] Cylinder042
  Angle = 360
  AttacherType = Attacher::AttachEngine3D
  Height = 10
  Placement = pos=(112,-13,43) rot=(0,0,1;0rad)
  Radius = 3
FEATURE [Part::Cylinder] Cylinder043
  Angle = 360
  AttacherType = Attacher::AttachEngine3D
  Height = 10
  Placement = pos=(5,-13,43) rot=(0,0,1;0rad)
  Radius = 3
FEATURE [Part::Cylinder] Cylinder044
  Angle = 360
  AttacherType = Attacher::AttachEngine3D
  Height = 10
  Placement = pos=(5,50,43) rot=(0,0,1;0rad)
  Radius = 3
FEATURE [Part::MultiFuse] Fusion010004007026009007004010029
  Shapes = -> [Cylinder038,Cylinder037,Cylinder035,Cylinder034,Cylinder033,Cylinder036]
FEATURE [Part::MultiFuse] Fusion010004007026009007004010030
  Placement = pos=(0,0,3.5) rot=(0,0,1;0rad)
  Shapes = -> [Cylinder044,Cylinder041,Cylinder040,Cylinder043,Cylinder039,Cylinder042]
FEATURE [Part::Feature] Chamfer013006001  label="Chamfer013007"
  Placement = pos=(22,1,0) rot=(0,0,1;0rad)
  shape: bbox 3 x 40 x 4 mm, 9 faces (baked)
FEATURE [Part::Feature] Chamfer013006002  label="Chamfer013008"
  Placement = pos=(22,68,0) rot=(0,0,1;0rad)
  shape: bbox 3 x 40 x 4 mm, 9 faces (baked)
FEATURE [Part::Feature] Chamfer013006003  label="Chamfer013009"
  Placement = pos=(22,138,0) rot=(0,0,1;0rad)
  shape: bbox 3 x 40 x 4 mm, 9 faces (baked)
FEATURE [Part::Feature] Chamfer013006004  label="Chamfer013010"
  Placement = pos=(47,167,0) rot=(0,0,1;4.71239rad)
  shape: bbox 40 x 3 x 4 mm, 9 faces (baked)
FEATURE [Part::Feature] Chamfer013006005  label="Chamfer013011"
  Placement = pos=(95,104,0) rot=(0,0,1;3.14159rad)
  shape: bbox 3 x 40 x 4 mm, 9 faces (baked)
FEATURE [Part::Feature] Chamfer013006006  label="Chamfer013012"
  Placement = pos=(95,37,0) rot=(0,0,1;3.14159rad)
  shape: bbox 3 x 40 x 4 mm, 9 faces (baked)
FEATURE [Part::MultiFuse] Fusion010004007026009007004010032
  Shapes = -> [Chamfer013006006,Chamfer013006005,Chamfer013006003,Chamfer013006004,Chamfer013006002,Chamfer013006001]
FEATURE [Part::Box] Box050  label="Cube034"
  AttacherType = Attacher::AttachEngine3D
  Height = 6
  Length = 12
  Placement = pos=(7.5,186,35) rot=(0,0,1;0rad)
  Width = 4
FEATURE [Part::Box] Box051  label="Cube035"
  AttacherType = Attacher::AttachEngine3D
  Height = 8
  Length = 16
  Placement = pos=(5.5,186,35) rot=(0,0,1;0rad)
  Width = 4
FEATURE [Part::Chamfer] Chamfer013006007
  Base = -> Box051
  Edges = 2 edges r=2: [Edge2,Edge6]
FEATURE [Part::Chamfer] Chamfer013006008
  Base = -> Chamfer013006007
  Edges = 10 edges r=1: [Edge1,Edge4,Edge5,Edge6,Edge8,Edge9,Edge11,Edge14,Edge15,Edge16]
FEATURE [Part::MultiFuse] Fusion010004007026009007004010033
  Shapes = -> [Box040,Chamfer013006008]
FEATURE [Part::Chamfer] Chamfer013006009
  Base = -> Box050
  Edges = 2 edges r=1: [Edge2,Edge6]
FEATURE [Part::Cut] Cut003002006013012005
  Base = -> Fusion010004007026009007004010033
  Tool = -> Chamfer013006009
FEATURE [Part::MultiFuse] Fusion010004007026009007004010030003
  Shapes = -> [Cut003002006013012005,Box038,Fillet,Cut003002006013012004,Box047,Box045,Box046,Box044,Fusion010004007026009007004010026,Fusion010004007026009007004010032]
FEATURE [Part::Chamfer] Chamfer013006010
  Base = -> Fusion010004007026009007004010030003
  Edges = 5 edges r=1: [Edge28,Edge29,Edge67,Edge68,Edge118]
FEATURE [Part::MultiFuse] Fusion010004007026009007004010030004
  Shapes = -> [Fusion010004007026009007004010028,Chamfer013006010]
FEATURE [Part::Feature] Fusion010004007026009007004010029001  label="Fusion010004007026009007004010030005"
  Placement = pos=(0,0,-6.5) rot=(0,0,1;0rad)
  shape: bbox 110.3 x 135.3 x 10 mm, 18 faces, 6 solids (baked)
FEATURE [Part::MultiFuse] Fusion010004007026009007004010030005  label="Fusion010004007026009007004010030006"
  Placement = pos=(0,0,-3) rot=(0,0,1;0rad)
  Shapes = -> [Fusion010004007026009007004010029001,Fusion010004007026009007004010029]
FEATURE [Part::Cut] Cut003002006013012006
  Base = -> Fusion010004007026009007004010030004
  Tool = -> Fusion010004007026009007004010030005
FEATURE [Part::Feature] Cut003002006013012006001  label="Cut003002006013012007"
  shape: bbox 117 x 208 x 14 mm, 899 faces (baked)
FEATURE [Part::Chamfer] Chamfer013006011
  Base = -> Cut003002006013012006001
  Edges = 7 edges r=1: [Edge2612,Edge2614,Edge2619,Edge2620,Edge2621,Edge2622,Edge2623]
FEATURE [Part::Cut] Cut003002006013012006002
  Base = -> Chamfer013006011
  Tool = -> Fusion010004007026009007004010030
FEATURE [Part::Box] Box052  label="Cube036"
  AttacherType = Attacher::AttachEngine3D
  Height = 10
  Length = 24
  Placement = pos=(10,0,42) rot=(0,0,1;0rad)
  Width = 2
FEATURE [Part::Box] Box053  label="Cube037"
  AttacherType = Attacher::AttachEngine3D
  Height = 10
  Length = 24
  Placement = pos=(10,4,42) rot=(0,0,1;0rad)
  Width = 2
FEATURE [Part::Box] Box054  label="Cube038"
  AttacherType = Attacher::AttachEngine3D
  Height = 10
  Length = 24
  Placement = pos=(10,8,42) rot=(0,0,1;0rad)
  Width = 2
FEATURE [Part::Box] Box055  label="Cube039"
  AttacherType = Attacher::AttachEngine3D
  Height = 10
  Length = 24
  Placement = pos=(10,12,42) rot=(0,0,1;0rad)
  Width = 2
FEATURE [Part::Box] Box056  label="Cube040"
  AttacherType = Attacher::AttachEngine3D
  Height = 10
  Length = 24
  Placement = pos=(10,16,42) rot=(0,0,1;0rad)
  Width = 2
FEATURE [Part::Box] Box057  label="Cube041"
  AttacherType = Attacher::AttachEngine3D
  Height = 10
  Length = 24
  Placement = pos=(10,20,42) rot=(0,0,1;0rad)
  Width = 2
FEATURE [Part::MultiFuse] Fusion010004007026009007004010030006  label="Fusion010004007026009007004010030007"
  Shapes = -> [Box057,Box056,Box055,Box054,Box053,Box052]
FEATURE [Part::Feature] Fusion010004007026009007004010030006001  label="Fusion010004007026009007004010030008"
  Placement = pos=(0,29,0) rot=(0,0,1;0rad)
  shape: bbox 24 x 22 x 10 mm, 36 faces, 6 solids (baked)
FEATURE [Part::Feature] Fusion010004007026009007004010030006002  label="Fusion010004007026009007004010030009"
  Placement = pos=(0,58,0) rot=(0,0,1;0rad)
  shape: bbox 24 x 22 x 10 mm, 36 faces, 6 solids (baked)
FEATURE [Part::Feature] Fusion010004007026009007004010030006003  label="Fusion010004007026009007004010030010"
  Placement = pos=(0,87,0) rot=(0,0,1;0rad)
  shape: bbox 24 x 22 x 10 mm, 36 faces, 6 solids (baked)
FEATURE [Part::Feature] Fusion010004007026009007004010030006004  label="Fusion010004007026009007004010030011"
  Placement = pos=(0,116,0) rot=(0,0,1;0rad)
  shape: bbox 24 x 22 x 10 mm, 36 faces, 6 solids (baked)
FEATURE [Part::Feature] Fusion010004007026009007004010030006005  label="Fusion010004007026009007004010030012"
  Placement = pos=(0,145,0) rot=(0,0,1;0rad)
  shape: bbox 24 x 22 x 10 mm, 36 faces, 6 solids (baked)
FEATURE [Part::MultiFuse] Fusion010004007026009007004010030006006
  Shapes = -> [Fusion010004007026009007004010030006005,Fusion010004007026009007004010030006,Fusion010004007026009007004010030006004,Fusion010004007026009007004010030006003,Fusion010004007026009007004010030006002,Fusion010004007026009007004010030006001]
FEATURE [Part::Cut] Cut003002006013012006003
  Base = -> Cut003002006013012006002
  Tool = -> Fusion010004007026009007004010030006006
FEATURE [Part::Feature] Chamfer013006012001  label="Chamfer013006013"
  Placement = pos=(18,-9,41) rot=(0,0,1;0rad)
  shape: bbox 7 x 2 x 4 mm, 12 faces (baked)
FEATURE [Part::Feature] Chamfer013006012002  label="Chamfer013006014"
  Placement = pos=(43,-9,41) rot=(0,0,1;0rad)
  shape: bbox 7 x 2 x 4 mm, 12 faces (baked)
FEATURE [Part::Feature] Chamfer013006012003  label="Chamfer013006015"
  Placement = pos=(73,-9,41) rot=(0,0,1;0rad)
  shape: bbox 7 x 2 x 4 mm, 12 faces (baked)
FEATURE [Part::Feature] Cut018002001  label="wire-route"
  Placement = pos=(61.5,91,46.5) rot=(0,1,0;3.14159rad)
  shape: bbox 8 x 11 x 9 mm, 18 faces (baked)
FEATURE [Part::Feature] Cut003002006013012006004  label="wire-route001"
  Placement = pos=(61.5,122,46.5) rot=(0,1,0;3.14159rad)
  shape: bbox 8 x 11 x 9 mm, 18 faces (baked)
FEATURE [Part::Feature] Cut003002006013012006005  label="wire-route002"
  Placement = pos=(61.5,35,46.5) rot=(0,1,0;3.14159rad)
  shape: bbox 8 x 11 x 9 mm, 18 faces (baked)
FEATURE [Part::Feature] Cut003002006013012006006  label="wire-route003"
  Placement = pos=(34.5,144,46.5) rot=(0,1,0;3.14159rad)
  shape: bbox 8 x 11 x 9 mm, 18 faces (baked)
FEATURE [Part::Feature] Cut003002006013012006007  label="wire-route004"
  Placement = pos=(66,7,46.5) rot=(-0.707107,0.707107,0;3.14159rad)
  shape: bbox 11 x 8 x 9 mm, 18 faces (baked)
FEATURE [Part::Feature] Cut003002006013012006008  label="wire-route005"
  Placement = pos=(76.5,-51,46.5) rot=(0.707107,-0.707107,0;3.14159rad)
  shape: bbox 11 x 8 x 9 mm, 18 faces (baked)
FEATURE [Part::MultiFuse] Fusion010004007026009007004010030006007
  Shapes = -> [Cut003002006013012006008,Cut003002006013012006007,Cut003002006013012006006,Cut003002006013012006005,Cut003002006013012006004,Cut018002001,Chamfer013006012003,Chamfer013006012002,Chamfer013006012001]
FEATURE [Part::Box] Box058  label="Cube042"
  AttacherType = Attacher::AttachEngine3D
  Height = 7
  Length = 2
  Placement = pos=(107,45,30.5) rot=(0,0,1;0rad)
  Width = 10
FEATURE [Part::Box] Box059  label="Cube043"
  AttacherType = Attacher::AttachEngine3D
  Height = 7
  Length = 3
  Placement = pos=(107,45,37.5) rot=(0,0,1;0rad)
  Width = 10
FEATURE [Part::Chamfer] Chamfer013006012004
  Base = -> Box059
  Edges = 1 edges r=1: [Edge8]
FEATURE [Part::MultiFuse] Fusion010004007026009007004010030006008
  Placement = pos=(0,0,0.5) rot=(0,0,1;0rad)
  Shapes = -> [Box058,Chamfer013006012004]
FEATURE [Part::Cut] Cut003002006013012006009
  Base = -> Cut003002006013012006003
  Tool = -> Fusion010004007026009007004010030006008
FEATURE [Part::MultiFuse] Fusion010004007026009007004010030006009
  Shapes = -> [Cut003002006013012006009,Fusion010004007026009007004010030006007]
